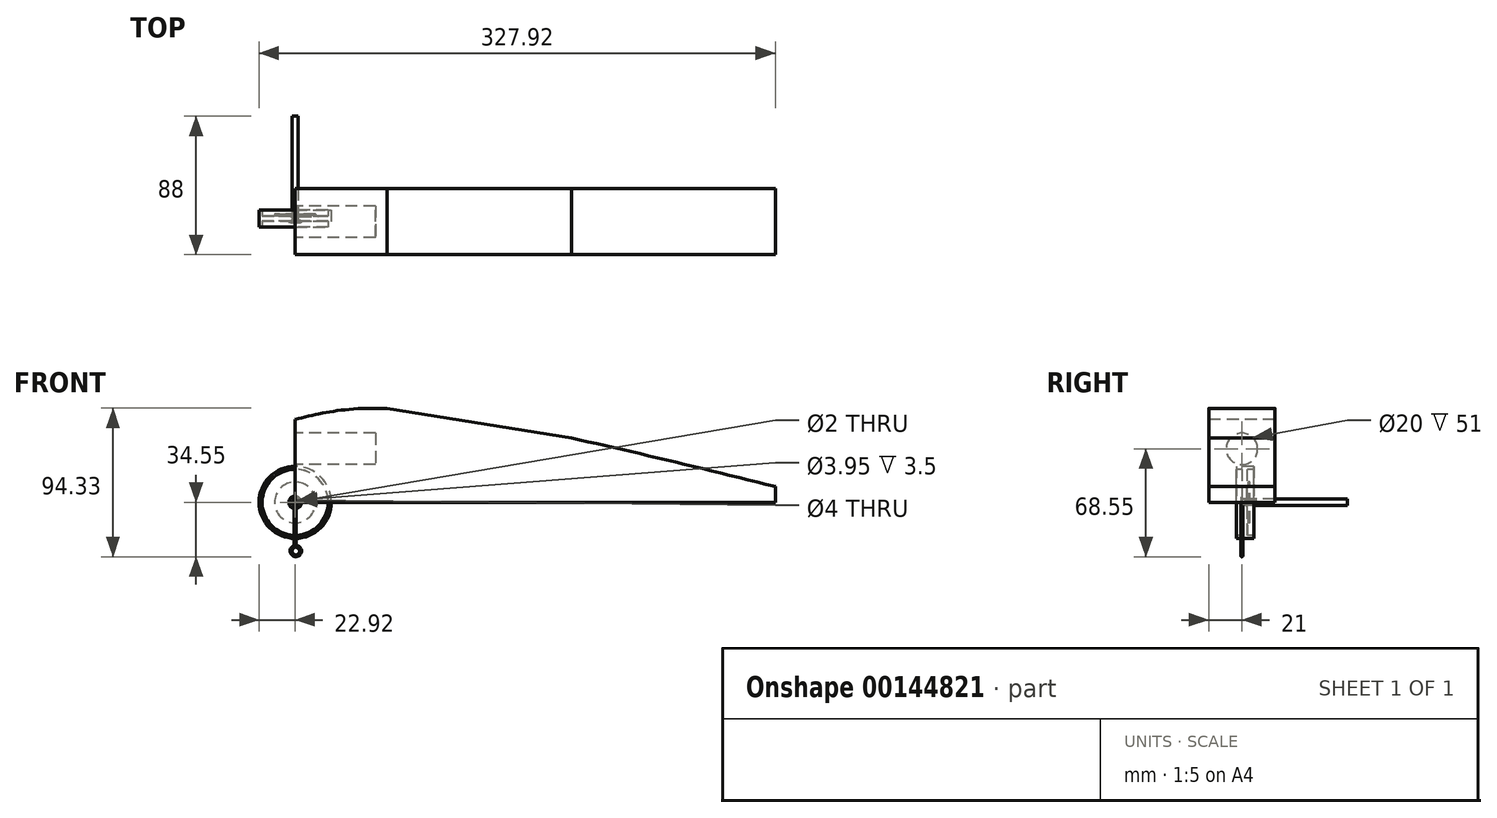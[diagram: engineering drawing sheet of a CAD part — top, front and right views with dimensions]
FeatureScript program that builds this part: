
annotation { "Feature Type Name" : "Feature", "Feature Type Description" : "" }
export const myFeature = defineFeature(function(context is Context, id is Id, definition is map)
    precondition{}
    {
        {
            var Q0;
            Q0=qCreatedBy(makeId("Front.planeOp"),FACE);
            var sketch = newSketch(context, id + "F0", { "sketchPlane" : qUnion([Q0])});
            skLineSegment(sketch, "E0", {"start": v(0, 0) * mm, "end": v(305, 0) * mm});
            skLineSegment(sketch, "E1", {"start": v(305, 0) * mm, "end": v(305, 20) * mm});
            skLineSegment(sketch, "E2", {"start": v(305, 20) * mm, "end": v(0, 69) * mm});
            skLineSegment(sketch, "E3", {"start": v(0, 69) * mm, "end": v(0, 0) * mm});
            skSolve(sketch);
        }
        {
            var Q0;
            Q0=qSketchRegion(id+"F0",true);
            extrude(context, id + "F1", {"entities" : qUnion([Q0]), "endBound" : BoundingType.SYMMETRIC, "depth" : 42 * mm});
        }
        {
            var Q0;
            Q0=qCreatedBy(makeId("Front.planeOp"),FACE);
            var sketch = newSketch(context, id + "F2", { "sketchPlane" : qUnion([Q0])});
            skCircle(sketch, "E4", {"center": v(0, 0) * mm, "radius": 4 * mm});
            skCircle(sketch, "E5", {"center": v(0, 0) * mm, "radius": 2 * mm});
            skSolve(sketch);
        }
        {
            var Q0;
            Q0=makeQuery(id+"F2.imprint","IMPRINT",FACE,{"disambiguationData":[TD([[makeQuery(id+"F2.imprint","IMPRINT",EDGE,{"derivedFrom":sQuery(id+"F2.wireOp",EDGE,"E4")}),1.0]])]});
            extrude(context, id + "F3", {"entities" : qUnion([Q0]), "endBound" : BoundingType.SYMMETRIC, "depth" : .33333333333333331968 * mm});
        }
        {
            var Q0;
            Q0=qCreatedBy(makeId("Right.planeOp"),FACE);
            var sketch = newSketch(context, id + "F4", { "sketchPlane" : qUnion([Q0])});
            skLineSegment(sketch, "E6", {"start": v(0, 0) * mm, "end": v(4.06, 0) * mm, "construction": true});
            skLineSegment(sketch, "E7", {"start": v(0, 1.98) * mm, "end": v(3.5, 1.98) * mm});
            skLineSegment(sketch, "E8", {"start": v(3.5, 1.98) * mm, "end": v(3.5, 2.98) * mm});
            skLineSegment(sketch, "E9", {"start": v(0, 1.98) * mm, "end": v(0, 2.98) * mm});
            skLineSegment(sketch, "E10", {"start": v(0, 2.98) * mm, "end": v(0.25, 2.98) * mm});
            skLineSegment(sketch, "E11", {"start": v(3.5, 2.98) * mm, "end": v(3.25, 2.98) * mm});
            skLineSegment(sketch, "E12", {"start": v(0.25, 2.98) * mm, "end": v(3.25, 2.98) * mm});
            skLineSegment(sketch, "E13", {"start": v(3.25, 2.98) * mm, "end": v(3.5, 20.97) * mm});
            skLineSegment(sketch, "E14", {"start": v(0.25, 2.98) * mm, "end": v(0.5, 20.97) * mm});
            skLineSegment(sketch, "E15", {"start": v(3.5, 20.97) * mm, "end": v(7.5, 20.92) * mm});
            skLineSegment(sketch, "E16", {"start": v(0.5, 20.97) * mm, "end": v(-3.5, 21.03) * mm});
            skLineSegment(sketch, "E17", {"start": v(7.5, 20.92) * mm, "end": v(7.53, 22.92) * mm});
            skLineSegment(sketch, "E18", {"start": v(-3.5, 21.03) * mm, "end": v(-3.5, 22.92) * mm});
            skLineSegment(sketch, "E19", {"start": v(-3.5, 22.92) * mm, "end": v(7.53, 22.92) * mm});
            skSolve(sketch);
        }
        {
            var Q0;
            Q0=qSketchRegion(id+"F4",true);
            var Q1;
            Q1=sQuery(id+"F4.wireOp",EDGE,"E6");
            revolve(context, id + "F5", {"entities" : qUnion([Q0]), "axis" : qUnion([Q1]), "revolveType" : RevolveType.FULL});
        }
        {
            var Q0;
            Q0=qCreatedBy(makeId("Front.planeOp"),FACE);
            var sketch = newSketch(context, id + "F6", { "sketchPlane" : qUnion([Q0])});
            skLineSegment(sketch, "E20", {"start": v(0, 0) * mm, "end": v(0, -27) * mm});
            skPoint(sketch, "E21.visualSharp", {"position": v(0, -33.93) * mm});
            skArc(sketch, "E21.filletArc", {"start": v(0, -27) * mm, "mid": v(0.24, -27.65) * mm, "end": v(0.85, -27.99) * mm});
            skArc(sketch, "E22", {"start": v(-0.7, -28.17) * mm, "mid": v(0.75, -33.94) * mm, "end": v(0.85, -27.99) * mm});
            skSolve(sketch);
        }
        {
            var Q0;
            Q0=qCreatedBy(makeId("Top.planeOp"),FACE);
            var sketch = newSketch(context, id + "F7", { "sketchPlane" : qUnion([Q0])});
            skCircle(sketch, "E23", {"center": v(0, 0) * mm, "radius": 0.6 * mm});
            skSolve(sketch);
        }
        {
            var Q0;
            Q0=makeQuery(id+"F7.imprint","IMPRINT",FACE,{"disambiguationData":[TD([[makeQuery(id+"F7.imprint","IMPRINT",EDGE,{"derivedFrom":sQuery(id+"F7.wireOp",EDGE,"E23")}),1.0]])]});
            var Q1;
            Q1=sQuery(id+"F6.wireOp",EDGE,"E20");
            var Q2;
            Q2=sQuery(id+"F6.wireOp",EDGE,"E21.filletArc");
            var Q3;
            Q3=sQuery(id+"F6.wireOp",EDGE,"E22");
            sweep(context, id + "F8", {"profiles" : qUnion([Q0]), "path" : qUnion([Q1, Q2, Q3])});
        }
        {
            var Q0;
            Q0=qCreatedBy(makeId("Right.planeOp"),FACE);
            var sketch = newSketch(context, id + "F9", { "sketchPlane" : qUnion([Q0])});
            skLineSegment(sketch, "E24", {"start": v(0, 0) * mm, "end": v(9, 0) * mm, "construction": true});
            skLineSegment(sketch, "E25", {"start": v(0, 2) * mm, "end": v(9, 2) * mm});
            skLineSegment(sketch, "E26", {"start": v(5, 2) * mm, "end": v(5, 13) * mm});
            skLineSegment(sketch, "E27", {"start": v(5, 13) * mm, "end": v(4, 13) * mm});
            skLineSegment(sketch, "E28", {"start": v(4, 13) * mm, "end": v(4, 2) * mm});
            skPoint(sketch, "E28.endSnap0", {"position": v(4.5, 2) * mm});
            skLineSegment(sketch, "E29", {"start": v(9, 2) * mm, "end": v(9, 1) * mm});
            skLineSegment(sketch, "E30", {"start": v(9, 1) * mm, "end": v(0, 1) * mm});
            skLineSegment(sketch, "E31", {"start": v(0, 1) * mm, "end": v(0, 2) * mm});
            skSolve(sketch);
        }
        {
            var Q0;
            Q0=qSketchRegion(id+"F9",true);
            var Q1;
            Q1=sQuery(id+"F9.wireOp",EDGE,"E24");
            revolve(context, id + "F10", {"entities" : qUnion([Q0]), "axis" : qUnion([Q1]), "revolveType" : RevolveType.FULL});
        }
        {
            var Q0;
            Q0=qCreatedBy(makeId("Right.planeOp"),FACE);
            var sketch = newSketch(context, id + "F11", { "sketchPlane" : qUnion([Q0])});
            skLineSegment(sketch, "E32", {"start": v(0, 0) * mm, "end": v(67, 0) * mm});
            skLineSegment(sketch, "E33", {"start": v(0, 0) * mm, "end": v(67, 0) * mm, "construction": true});
            skLineSegment(sketch, "E34", {"start": v(67, 0) * mm, "end": v(67, 2) * mm});
            skLineSegment(sketch, "E35", {"start": v(67, 2) * mm, "end": v(0, 2) * mm});
            skLineSegment(sketch, "E36", {"start": v(0, 2) * mm, "end": v(0, 0) * mm});
            skSolve(sketch);
        }
        {
            var Q0;
            Q0=qSketchRegion(id+"F11",true);
            var Q1;
            Q1=sQuery(id+"F11.wireOp",EDGE,"E33");
            revolve(context, id + "F12", {"entities" : qUnion([Q0]), "axis" : qUnion([Q1]), "revolveType" : RevolveType.FULL});
        }
        {
            var Q0;
            Q0=makeQuery(id+"F1.opExtrude","SWEPT_FACE",FACE,{"disambiguationData":[OSD([sQuery(id+"F0.wireOp",EDGE,"E3")])]});
            var sketch = newSketch(context, id + "F13", { "sketchPlane" : qUnion([Q0])});
            skCircle(sketch, "E37", {"center": v(0, 34) * mm, "radius": 10 * mm});
            skSolve(sketch);
        }
        {
            var Q0;
            Q0=makeQuery(id+"F13.imprint","IMPRINT",FACE,{"disambiguationData":[TD([[makeQuery(id+"F13.imprint","IMPRINT",EDGE,{"derivedFrom":sQuery(id+"F13.wireOp",EDGE,"E37")}),1.0]])]});
            extrude(context, id + "F14", {"entities" : qUnion([Q0]), "operationType" : NewBodyOperationType.REMOVE, "oppositeDirection" : true, "depth" : 51 * mm});
        }
        {
            var Q0;
            Q0=makeQuery(id+"F1.opExtrude","CAP_FACE",FACE,{"disambiguationData":[OSD([sQuery(id+"F0.wireOp",EDGE,"E0"),sQuery(id+"F0.wireOp",EDGE,"E1"),sQuery(id+"F0.wireOp",EDGE,"E2"),sQuery(id+"F0.wireOp",EDGE,"E3")])],"isStart":false});
            var sketch = newSketch(context, id + "F15", { "sketchPlane" : qUnion([Q0])});
            skLineSegment(sketch, "E38.0", {"start": v(0, 0) * mm, "end": v(305, 0) * mm});
            skLineSegment(sketch, "E39.0", {"start": v(305, 20) * mm, "end": v(0, 69) * mm});
            skLineSegment(sketch, "E40.0", {"start": v(305, 0) * mm, "end": v(305, 20) * mm});
            skFitSpline(sketch, "E41", {"points": [v(0, 52.65) * mm, v(58.46, 59.6) * mm, v(305, 10) * mm], "startDerivative": vector(148.87, 36.82) * mm, "endDerivative": vector(428.69, -105.6) * mm});
            skSolve(sketch);
        }
        {
            var Q0;
            {var subQ0=sQuery(id+"F15.wireOp",EDGE,"E39.0");var subQ1=makeQuery(id+"F1.opExtrude","CAP_EDGE",EDGE,{"disambiguationData":[OSD([sQuery(id+"F0.wireOp",EDGE,"E3")])],"isStart":false});var subQ2=makeQuery(id+"F15.imprint","INTERSECT",VERTEX,{"derivedFrom":[subQ1,subQ0]});Q0=makeQuery(id+"F15.imprint","IMPRINT",FACE,{"disambiguationData":[TD([[makeQuery(id+"F15.imprint","IMPRINT",EDGE,{"disambiguationData":[TD([[subQ2,1.0]])],"derivedFrom":subQ0}),1.0]])]});}
            var Q1;
            {var subQ0=sQuery(id+"F15.wireOp",EDGE,"E40.0");var subQ1=sQuery(id+"F15.wireOp",EDGE,"E39.0");var subQ2=makeQuery(id+"F15.imprint","INTERSECT",VERTEX,{"derivedFrom":[subQ1,subQ0]});Q1=makeQuery(id+"F15.imprint","IMPRINT",FACE,{"disambiguationData":[TD([[makeQuery(id+"F15.imprint","IMPRINT",EDGE,{"disambiguationData":[TD([[subQ2,-1.0]])],"derivedFrom":subQ1}),1.0]])]});}
            extrude(context, id + "F16", {"entities" : qUnion([Q0, Q1]), "operationType" : NewBodyOperationType.REMOVE, "endBound" : BoundingType.THROUGH_ALL, "oppositeDirection" : true, "depth" : 25 * mm});
        }
    });
